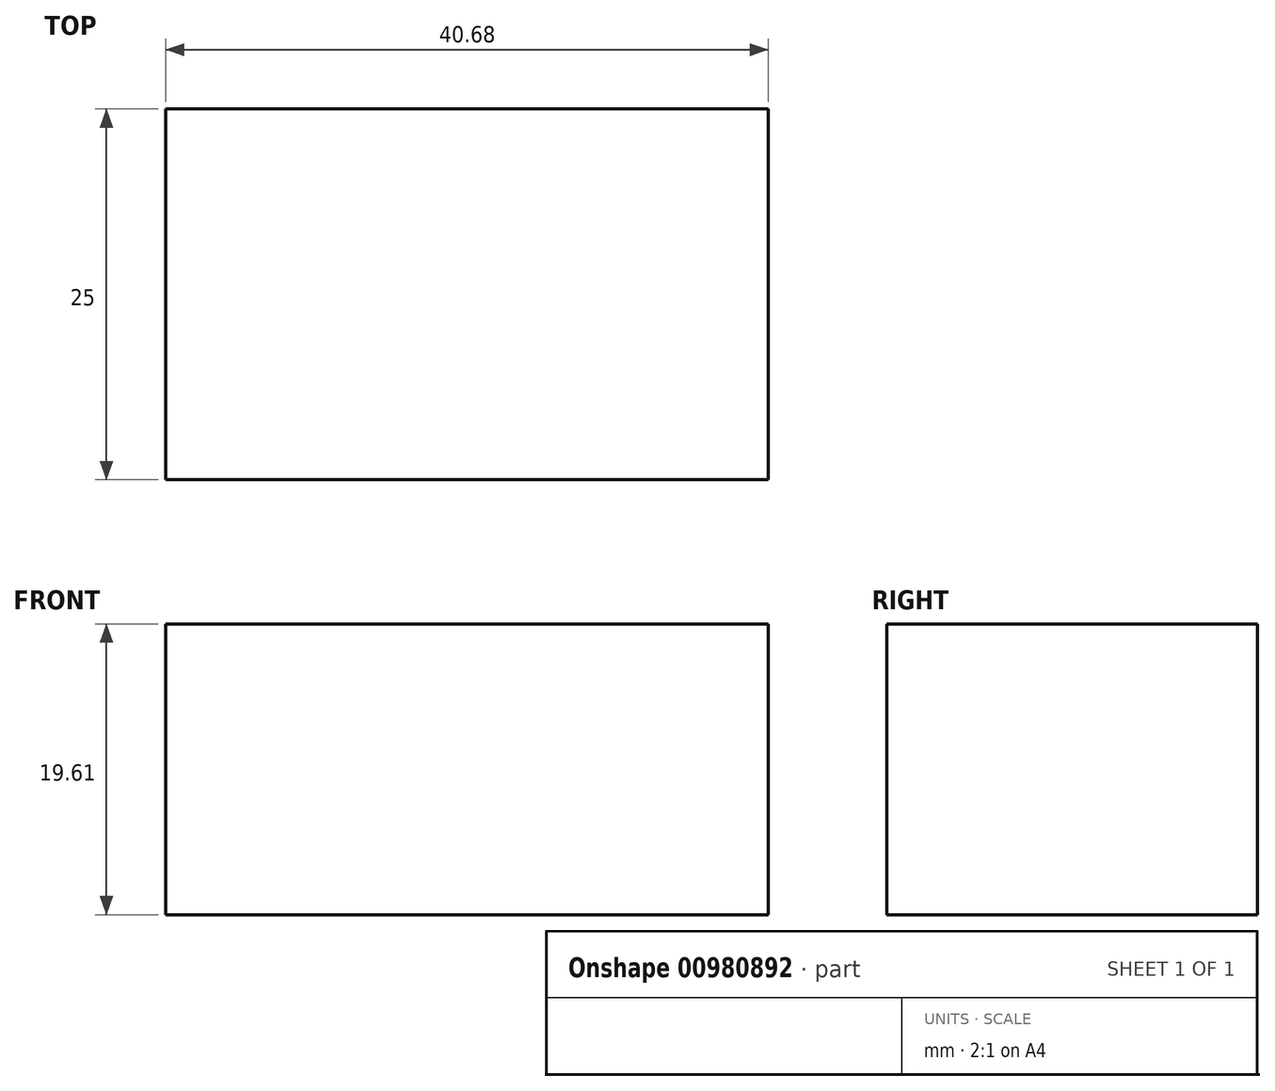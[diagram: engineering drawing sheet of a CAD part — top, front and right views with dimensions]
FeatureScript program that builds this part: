
annotation { "Feature Type Name" : "Feature", "Feature Type Description" : "" }
export const myFeature = defineFeature(function(context is Context, id is Id, definition is map)
    precondition{}
    {
        {
            var Q0;
            Q0=qCreatedBy(makeId("Front.planeOp"),FACE);
            var sketch = newSketch(context, id + "F0", { "sketchPlane" : qUnion([Q0])});
            skLineSegment(sketch, "E0.bottom", {"start": v(-51.22, 38.48) * mm, "end": v(-10.54, 38.48) * mm});
            skLineSegment(sketch, "E0.top", {"start": v(-51.22, 18.87) * mm, "end": v(-10.54, 18.87) * mm});
            skLineSegment(sketch, "E0.left", {"start": v(-51.22, 38.48) * mm, "end": v(-51.22, 18.87) * mm});
            skLineSegment(sketch, "E0.right", {"start": v(-10.54, 38.48) * mm, "end": v(-10.54, 18.87) * mm});
            skSolve(sketch);
        }
        {
            var Q0;
            Q0 = qSketchRegion(id + "F0", true);
            extrude(context, id + "F1", {"entities" : qUnion([Q0]), "depth" : 25 * mm, "offsetDistance" : 25 * mm});
        }
    });
